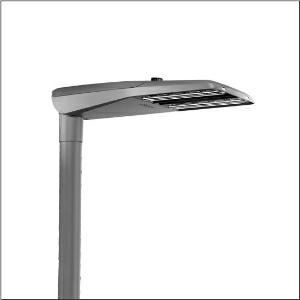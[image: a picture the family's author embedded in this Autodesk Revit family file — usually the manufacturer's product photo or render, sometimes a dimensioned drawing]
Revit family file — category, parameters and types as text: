
# Revit family: streetlight_sl_11_iq_midi___st1_2a_5xc3a51u08me_6b2b
name_source: partatom
category: Lighting Fixtures
units: mm (PartAtom-declared; Revit-internal decimal feet)

## family parameters
Cut with Voids When Loaded = No
Host = Face
Light Source = No
Part Type = Normal
Room Calculation Point = No
Round Connector Dimension = Use Diameter
Shared = No

## types (1)
- --- (1 x LED, 18110 lm, 122.7 W, 3000K)
    Apparent Load = 123 VA
    CIE Flux Codes = 32 70 96 100 100
    Color Rendering = 70
    Color Temperature = 3000K
    Default Elevation = 1800 mm
    Description = Streetlight SL 11 iQ midi, mast luminaire, primary light control with 3 zone facetted reflector, of plastic, silver coated, highly specular, primary optical cover: cover, of PMMA, transparent, light distribution: ST1.2a, light emission: direct distribution, primary light characteristic: asymmetric, installation type: post-top, side-entry, LED, High Power LED, rated luminous flux: 18.110lm, luminous efficacy: 148lm/W, light colour: 730, colour temperature: 3000K, control: presetting dimming logarithmic, Street-Remote, Auto-Match, Temp-Guard, Lumen-Switch, Night-Set, Smart-Wire, Light-Fading, Desk-Remote (wireless, voltage-free reading and setting of iQ features in the workshop via application-optimized NFC function/RFID function), optimised constant luminous flux control (CLO 2.0), with cable H07RN-F 5x 1.5mm², mains connection: 230..240V, AC, 50/60Hz, connection cable pre-assembled, cable length: 12,5m, start of lifetime: 123W, end of service life: 130W, reduction: 56W, luminaire housing, of diecast aluminium, powder-coated, Siteco® metallic grey (DB 702S), please order mast flange separately, inclination adjustable without tools: 0°, 5°, 10°, 15° (post-top) | 0°, -5°, -10°, -15° (side-entry), sealing non-destructively replaceable, multi-level sealing system, length: 780mm, width: 376mm, height: 118mm, mast flange for spigot size: 42mm (side-entry): 5XC10008XM4, 60/48mm (side-entry/post-top): 5XC10108XM2, 76/60mm (side-entry/post-top): 5XC10108XM1, equipment: Power, Smart Interface below, protection rating (complete): IP66, insulation class (complete): insulation class II (safety insulation), certification: CE, ENEC, VDE, UKCA, impact resistance: IK09, permissible operating ambient temperature for outdoor applications: -25..+50°C, standard-compliant lighting for roads and squares, Environmental Product Declaration (EPD) tested and certified by an independent institute, packaging unit: 1 piece

Light Distribution: ST1.2a
    Height = 118 mm
    Lamp = 1 x LED
    Lamp Light Flux = 18110 lm
    Lamp Power = 122.7 W
    Lamp count = 1
    Length = 780 mm
    Luminous efficacy = 148 lm/W
    Manufacturer = Siteco
    ModVariant = No
    Model = 5XC3A51U08ME
    Number of Poles = 1
    OnlyDefault = Yes
    Power Factor = 1
    Product Name = Streetlight SL 11 iQ midi | ST1.2a
    Product group = mast luminaire | pylon top
    ProductGroupID = 6100
    Protection Class = Protection class II
    Protection Degree = IP 66
    RLX_Detail_Level = 1
    RLX_Emergency_Light_Flux = 0 lm
    RLX_Emergency_Type = 0
    RLX_Emergency_Type_DB = No
    RlxData = <blob elided: 69853 chars, md5=34341be4>
    Socket = socket
    Standby Power = 0 W
    System Light Flux = 18111 lm
    System Power = 123 W
    Type Comments = factory setting: luminous flux: 100 % | dim-lin: 254 | 553 mA
    Type Image = l_1005968.jpg
    URL = http://relux.com
    VarID = @adj_064561
    Voltage = 0 V
    Weight = 0.00 kg
    Width = 376 mm

## geometry (parser evidence)
native form markers: Blend x4, Sweep x10
no freeform markers — native parametric forms only
